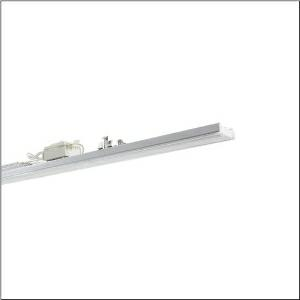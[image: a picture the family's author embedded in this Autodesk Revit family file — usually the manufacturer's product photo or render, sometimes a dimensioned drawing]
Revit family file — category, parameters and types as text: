
# Revit family: licross_21_recessed_mo_52tl12dv4fxg3s
name_source: partatom
category: Lighting Fixtures
units: mm (PartAtom-declared; Revit-internal decimal feet)

## family parameters
Cut with Voids When Loaded = No
Host = Face
Light Source = No
Part Type = Normal
Room Calculation Point = No
Round Connector Dimension = Use Diameter
Shared = No

## types (1)
- --- (1 x LED, 950 lm, 5.5 W, 4000K)
    Apparent Load = 6 VA
    CIE Flux Codes = 72 92 99 100 100
    Color Rendering = 80
    Color Temperature = 4000K
    Default Elevation = 1800 mm
    Description = Licross 21 Recessed MO, luminaire insert, of sheet steel, galvanised, coil coated, white, length: 2.250mm, width: 66mm, height: 67mm, LED rated luminous flux: 15.420lm, light colour: 840, SDCM (Standard Deviation of Colour Matching)MacAdam ≤ 3 SDCM (initial), control gear: DALI 2 (for two DALI lines), with plug, 6-pole, with phase selection, for trunking rail, 14-core, mains connection: 220..240V, AC, 50/60Hz, rated input power: 89W, for trunking rail, 14-core, internal wiring halogen-free, for emergency light function, converter,control gear: single battery element, battery: LiFePO4, 9Ah, primary optical cover: cover, of PMMA, light emission: direct distribution, primary light characteristic: symmetric, protection rating (complete): IP40, insulation class (complete): insulation class I (protective earthing), certification: CE, UKCA, protection symbol: D if used in an environment without relevant dust loads with corresponding accessories, impact resistance: IK06, permissible ambient temperature for indoor applications: +5..+35°C, standard: EN 60598-2-22, LABS conformity tested according to VDMA 24364:2018-05, reducing of maximum allowable ambient temperature of 5°C with ceiling mounting, corresponds to IFS (International Featured Standards) requirements for safety and quality in the food industry, The light source and the operating device comply with the requirements of the Ecodesign Regulation (EU) 2019/2020 and are replaceable in accordance with this regulation, packaging unit: 1 piece
    Height = 58 mm
    Lamp = 1 x LED
    Lamp Light Flux = 950 lm
    Lamp Power = 5.5 W
    Lamp count = 1
    Length = 2250 mm
    Luminous efficacy = 173 lm/W
    Manufacturer = Siteco
    ModVariant = No
    Model = 52TL12DV4FXG3S
    Mounting Place = Ceiling
    Mounting Type = Pendant
    Number of Poles = 1
    OnlyDefault = Yes
    Power Factor = 1
    Product Name = Licross 21 Recessed MO
    Product group = luminaire insert | ceiling pendant
    ProductGroupID = 901
    Protection Class = Protection class I
    Protection Degree = IP 40
    RLX_Detail_Level = 1
    RLX_Emergency_Light_Flux = 0 lm
    RLX_Emergency_Type = 0
    RLX_Emergency_Type_DB = No
    RlxData = <blob elided: 30069 chars, md5=4c76ceda>
    Socket = socket
    Standby Power = 0 W
    System Light Flux = 950 lm
    System Power = 6 W
    Type Comments = : emergency light operation: 3 h
    Type Image = l_1296930.jpg
    URL = http://relux.com
    VarID = @adj_110019
    Voltage = 0 V
    Weight = 0.00 kg
    Width = 66 mm

## geometry (parser evidence)
native form markers: Blend x4, Sweep x9
no freeform markers — native parametric forms only
